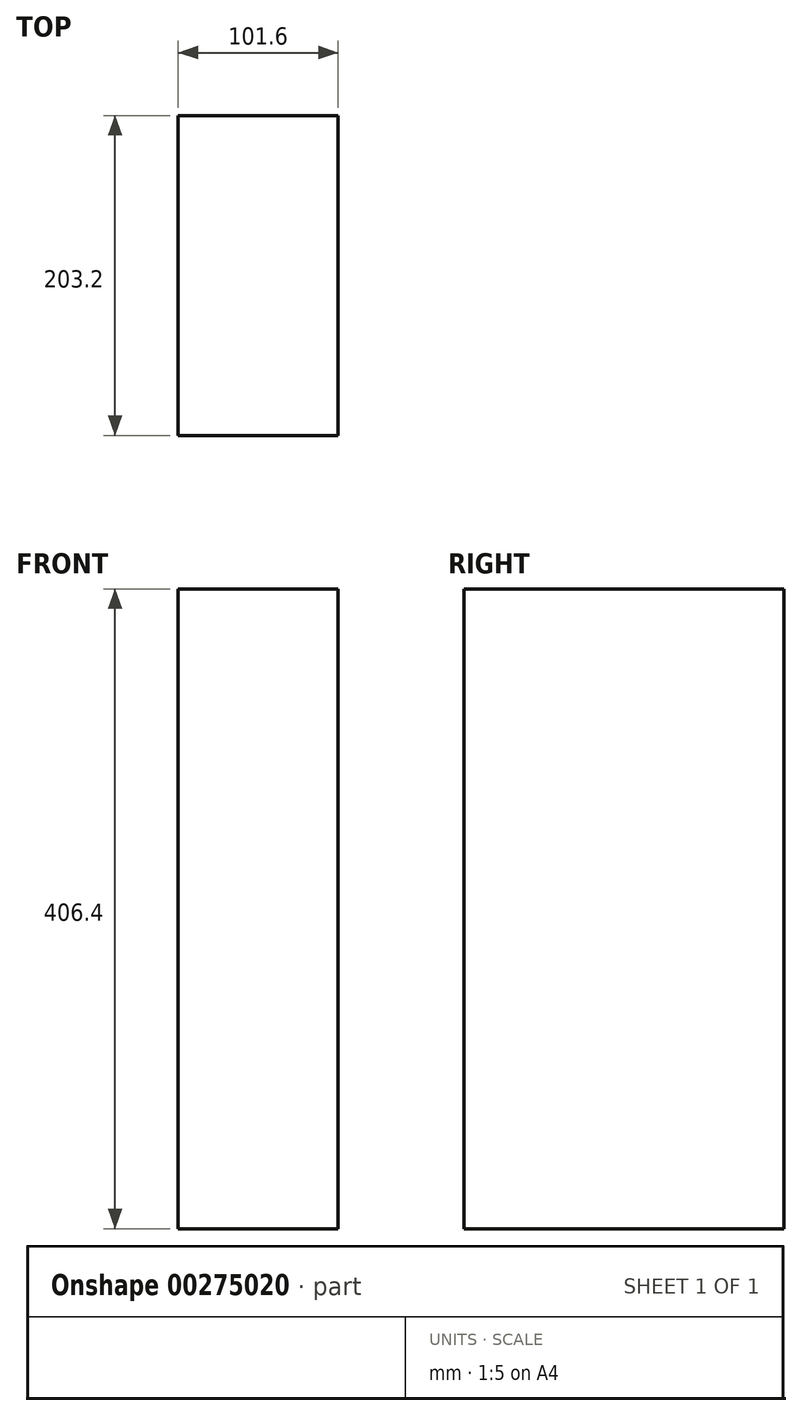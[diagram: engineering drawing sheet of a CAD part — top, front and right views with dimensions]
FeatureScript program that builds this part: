
annotation { "Feature Type Name" : "Feature", "Feature Type Description" : "" }
export const myFeature = defineFeature(function(context is Context, id is Id, definition is map)
    precondition{}
    {
        {
            var Q0;
            Q0=qCreatedBy(makeId("Top.planeOp"),FACE);
            var sketch = newSketch(context, id + "F0", { "sketchPlane" : qUnion([Q0])});
            skLineSegment(sketch, "E0.bottom", {"start": v(0, 0) * mm, "end": v(101.6, 0) * mm});
            skLineSegment(sketch, "E0.top", {"start": v(0, 203.2) * mm, "end": v(101.6, 203.2) * mm});
            skLineSegment(sketch, "E0.left", {"start": v(0, 0) * mm, "end": v(0, 203.2) * mm});
            skLineSegment(sketch, "E0.right", {"start": v(101.6, 0) * mm, "end": v(101.6, 203.2) * mm});
            skSolve(sketch);
        }
        {
            var Q0;
            Q0 = qSketchRegion(id + "F0", true);
            extrude(context, id + "F1", {"entities" : qUnion([Q0]), "depth" : 101.6 * mm, "offsetDistance" : 25.4 * mm});
        }
        {
            var Q0;
            Q0 = qSketchRegion(id + "F0", true);
            extrude(context, id + "F2", {"entities" : qUnion([Q0]), "operationType" : NewBodyOperationType.ADD, "depth" : 406.4 * mm, "offsetDistance" : 25.4 * mm});
        }
    });
